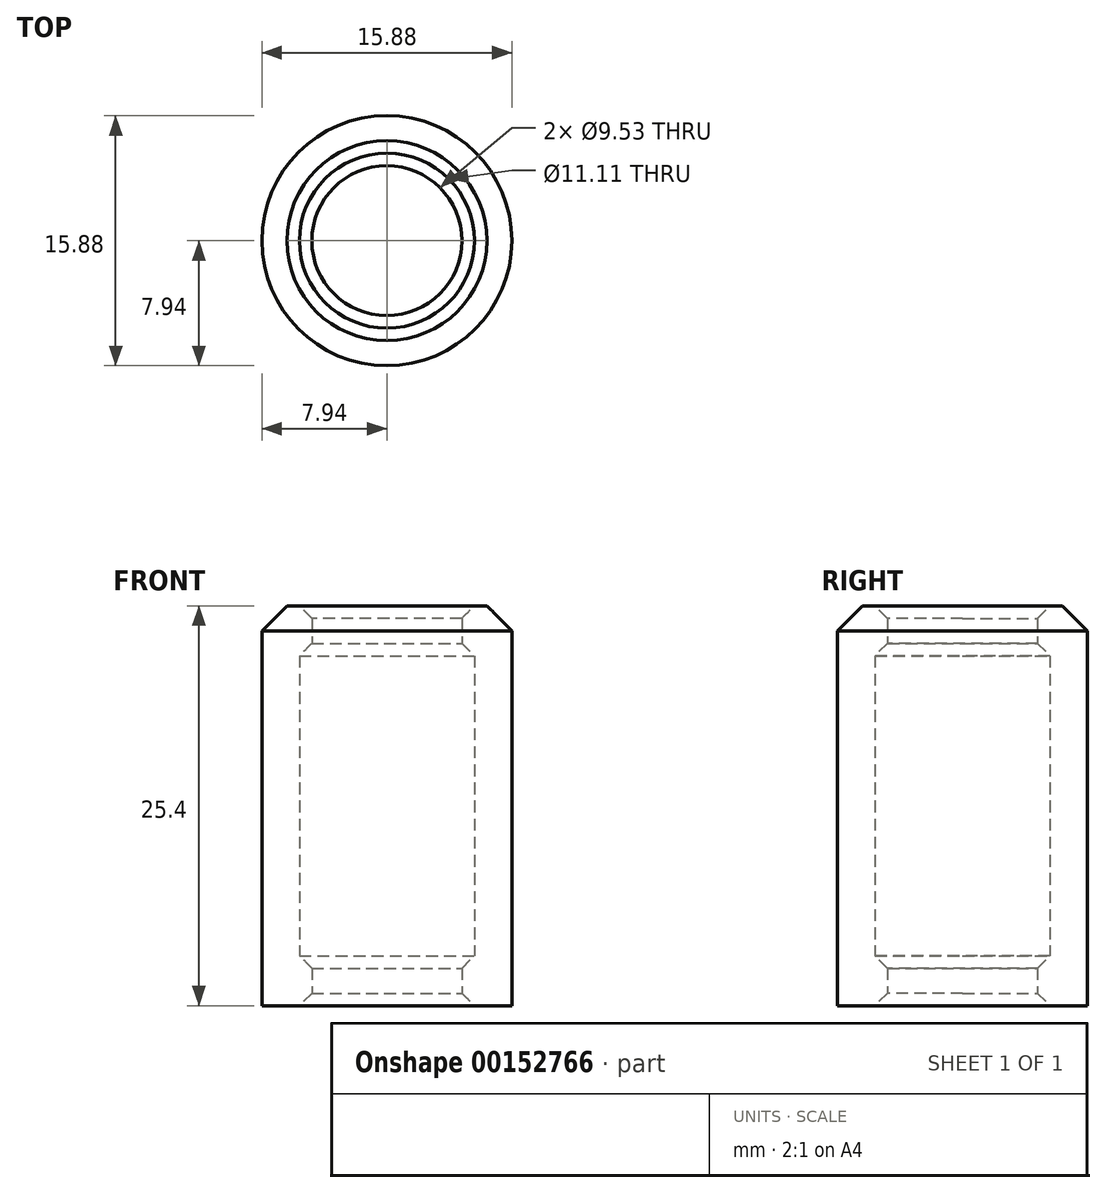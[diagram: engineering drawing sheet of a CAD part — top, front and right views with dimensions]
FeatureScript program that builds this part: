
annotation { "Feature Type Name" : "Feature", "Feature Type Description" : "" }
export const myFeature = defineFeature(function(context is Context, id is Id, definition is map)
    precondition{}
    {
        {
            var Q0;
            Q0=qCreatedBy(makeId("Top.planeOp"),FACE);
            var sketch = newSketch(context, id + "F0", { "sketchPlane" : qUnion([Q0])});
            skCircle(sketch, "E0", {"center": v(0, 0) * mm, "radius": 4.76 * mm});
            skCircle(sketch, "E1", {"center": v(0, 0) * mm, "radius": 7.94 * mm});
            skSolve(sketch);
        }
        {
            var Q0;
            Q0 = qSketchRegion(id + "F0", true);
            extrude(context, id + "F1", {"entities" : qUnion([Q0]), "depth" : 25.4 * mm});
        }
        {
            var Q0;
            Q0=makeQuery(id+"F1.opExtrude","CAP_EDGE",EDGE,{"disambiguationData":[OSD([sQuery(id+"F0.wireOp",EDGE,"E1")])],"isStart":false});
            chamfer(context, id + "F2", {"entities" : qUnion([Q0]), "width" : 1.59 * mm, "tangentPropagation" : true});
        }
        {
            var Q0;
            Q0=qCreatedBy(makeId("Front.planeOp"),FACE);
            var sketch = newSketch(context, id + "F3", { "sketchPlane" : qUnion([Q0])});
            skLineSegment(sketch, "E2", {"start": v(0, 0) * mm, "end": v(0, 3.18) * mm, "construction": true});
            skLineSegment(sketch, "E3", {"start": v(0, 25.4) * mm, "end": v(0, 22.23) * mm, "construction": true});
            skLineSegment(sketch, "E4.bottom", {"start": v(0, 3.18) * mm, "end": v(5.56, 3.18) * mm});
            skLineSegment(sketch, "E4.top", {"start": v(0, 22.23) * mm, "end": v(5.56, 22.23) * mm});
            skLineSegment(sketch, "E4.left", {"start": v(0, 3.18) * mm, "end": v(0, 22.23) * mm});
            skLineSegment(sketch, "E4.right", {"start": v(5.56, 3.18) * mm, "end": v(5.56, 22.23) * mm});
            skSolve(sketch);
        }
        {
            var Q0;
            Q0 = qSketchRegion(id + "F3", true);
            var Q1;
            Q1=makeQuery(id+"F1.opExtrude","SWEPT_FACE",FACE,{"disambiguationData":[OSD([sQuery(id+"F0.wireOp",EDGE,"E1")])]});
            revolve(context, id + "F4", {"operationType" : NewBodyOperationType.REMOVE, "entities" : qUnion([Q0]), "axis" : qUnion([Q1]), "revolveType" : RevolveType.FULL, "oppositeDirection" : true});
        }
        {
            var Q0;
            Q0=makeQuery(id+"F1.opExtrude","CAP_EDGE",EDGE,{"disambiguationData":[OSD([sQuery(id+"F0.wireOp",EDGE,"E0")])],"isStart":true});
            var Q1;
            Q1=makeQuery(id+"F4.boolean.opBoolean","INTERSECT",EDGE,{"derivedFrom":[makeQuery(id+"F1.opExtrude","SWEPT_FACE",FACE,{"disambiguationData":[OSD([sQuery(id+"F0.wireOp",EDGE,"E0")])]}),makeQuery(id+"F4.opRevolve","SWEPT_FACE",FACE,{"disambiguationData":[OSD([sQuery(id+"F3.wireOp",EDGE,"E4.bottom")])]})]});
            var Q2;
            Q2=makeQuery(id+"F4.boolean.opBoolean","INTERSECT",EDGE,{"derivedFrom":[makeQuery(id+"F1.opExtrude","SWEPT_FACE",FACE,{"disambiguationData":[OSD([sQuery(id+"F0.wireOp",EDGE,"E0")])]}),makeQuery(id+"F4.opRevolve","SWEPT_FACE",FACE,{"disambiguationData":[OSD([sQuery(id+"F3.wireOp",EDGE,"E4.top")])]})]});
            var Q3;
            Q3=makeQuery(id+"F1.opExtrude","CAP_EDGE",EDGE,{"disambiguationData":[OSD([sQuery(id+"F0.wireOp",EDGE,"E0")])],"isStart":false});
            chamfer(context, id + "F5", {"entities" : qUnion([Q0, Q1, Q2, Q3]), "width" : 0.8 * mm, "tangentPropagation" : true});
        }
    });
